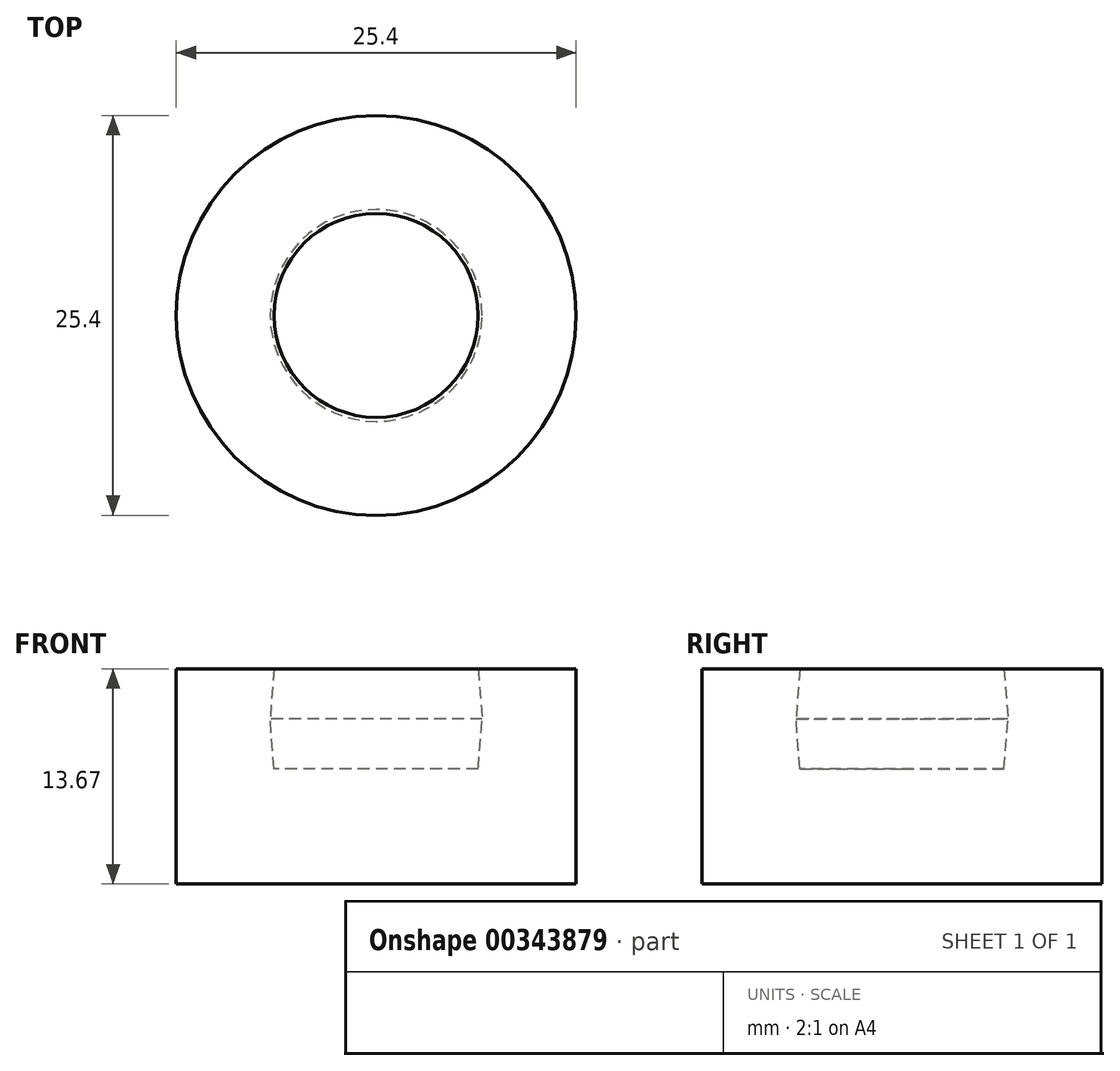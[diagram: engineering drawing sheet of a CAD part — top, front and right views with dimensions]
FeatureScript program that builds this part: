
annotation { "Feature Type Name" : "Feature", "Feature Type Description" : "" }
export const myFeature = defineFeature(function(context is Context, id is Id, definition is map)
    precondition{}
    {
        {
            var Q0;
            Q0=qCreatedBy(makeId("Front.planeOp"),FACE);
            var sketch = newSketch(context, id + "F0", { "sketchPlane" : qUnion([Q0])});
            skLineSegment(sketch, "E0", {"start": v(0, 0) * mm, "end": v(-12.7, 0) * mm});
            skLineSegment(sketch, "E1", {"start": v(-12.7, 0) * mm, "end": v(-12.7, 13.67) * mm});
            skLineSegment(sketch, "E2", {"start": v(-12.7, 13.67) * mm, "end": v(-6.48, 13.67) * mm});
            skLineSegment(sketch, "E3", {"start": v(-6.48, 13.67) * mm, "end": v(-6.48, 7.32) * mm});
            skLineSegment(sketch, "E4", {"start": v(-6.48, 7.32) * mm, "end": v(0, 7.32) * mm});
            skLineSegment(sketch, "E5", {"start": v(0, 7.32) * mm, "end": v(0, 0) * mm});
            skLineSegment(sketch, "E6", {"start": v(-6.48, 13.67) * mm, "end": v(-6.73, 10.5) * mm});
            skPoint(sketch, "E6.endSnap0", {"position": v(-6.48, 10.5) * mm});
            skLineSegment(sketch, "E7", {"start": v(-6.73, 10.5) * mm, "end": v(-6.48, 7.32) * mm});
            skSolve(sketch);
        }
        {
            var Q0;
            Q0=makeQuery(id+"F0.imprint","IMPRINT",FACE,{"disambiguationData":[TD([[makeQuery(id+"F0.imprint","IMPRINT",EDGE,{"derivedFrom":sQuery(id+"F0.wireOp",EDGE,"E0")}),-1.0]])]});
            var Q1;
            Q1=sQuery(id+"F0.wireOp",EDGE,"E5");
            revolve(context, id + "F1", {"entities" : qUnion([Q0]), "axis" : qUnion([Q1]), "revolveType" : RevolveType.FULL});
        }
    });
